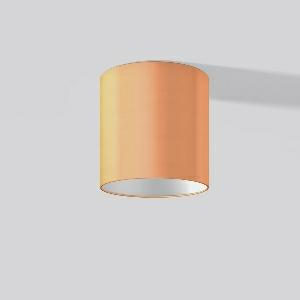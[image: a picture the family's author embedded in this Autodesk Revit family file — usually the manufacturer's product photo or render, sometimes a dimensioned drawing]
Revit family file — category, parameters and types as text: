
# Revit family: toledo_flatliner_901628_002_fee1
name_source: partatom
category: Lighting Fixtures
units: mm (PartAtom-declared; Revit-internal decimal feet)

## family parameters
Cut with Voids When Loaded = No
Host = Face
Light Source = No
Part Type = Normal
Room Calculation Point = No
Round Connector Dimension = Use Diameter
Shared = No

## types (1)
- 982299.002 (1 x LED Modul 830, 310 lm, 3000)
    Apparent Load = 5 VA
    CIE Flux Codes = 56 78 92 81 100
    Color Rendering = 80
    Color Temperature = 3000
    Default Elevation = 1800 mm
    Description = Series: TOLEDO FLATLINER
Decorative ceiling luminaire for interior decoration. Base luminaire prepared for the installation of fabric lampshade. Cylinder housing sheet steel, powder-coated. Housing: die cast aluminium and sheet steel, powder-coated. Bezel ring: die-cast aluminium, powder-coated. Lightguide and diffuser made of non-yellowing plastic (PMMA) opal matt. Modular design: With the basic luminaire, a square or cylindrical fabric lampshade must always be ordered separately. Fabric lampshades can be fitted to the basic luminaire without tools. Order satin finish diffuser as separate accessory. 
Colour: white
Diameter: 160 mm
Height: 65 mm
Lamp: LED
Socket: without socket
Colour temperature: 3000K
Colour rendering index (CRI): 80
System power: 5 W
Rated luminous flux: 310 lm
Luminous efficiency: 62 lm/W
Control gear: Regulated power supply
Protection class: II
Type of protection: IP 40
    Height = 65 mm
    Lamp = 1 x LED Modul 830
    Lamp Light Flux = 310 lm
    Lamp count = 1
    Length = 160 mm
    Lifetime = 50000 h
    Luminous efficacy = 62 lm/W
    Manufacturer = RZB
    ModVariant = No
    Model = 901628.002
    Mounting Place = Ceiling
    Mounting Type = Surface mounted
    Number of Poles = 1
    OnlyDefault = Yes
    Power Factor = 1
    Product Name = TOLEDO FLATLINER
    Product group = Surface mounted ceiling Fabric lampshade luminaires
    ProductGroupID = 313
    Protection Class = Protection class II
    Protection Degree = IP 40
    RLX_Detail_Level = 1
    RLX_Emergency_Light_Flux = 0 lm
    RLX_Emergency_Type = 0
    RLX_Emergency_Type_DB = No
    RlxData = <blob elided: 62397 chars, md5=2acb0fa6>
    Socket = socket
    Standby Power = 0 W
    System Light Flux = 310 lm
    System Power = 5 W
    Type Image = toledo_flatliner_anbau_rund_orange_odeckel.jpg
    URL = http://relux.com
    VarID = 982299_002_f7b2
    Voltage = 230 V
    Voltage Range = 220-240 V
    Weight = 0.00 kg
    Width = 0 mm  [stored 0 ft]

note: [stored X ft] marks values corroborated as IEEE doubles in the binary element streams (Revit-internal decimal feet)

## geometry (parser evidence)
native form markers: Blend x4, Sweep x12
no freeform markers — native parametric forms only
